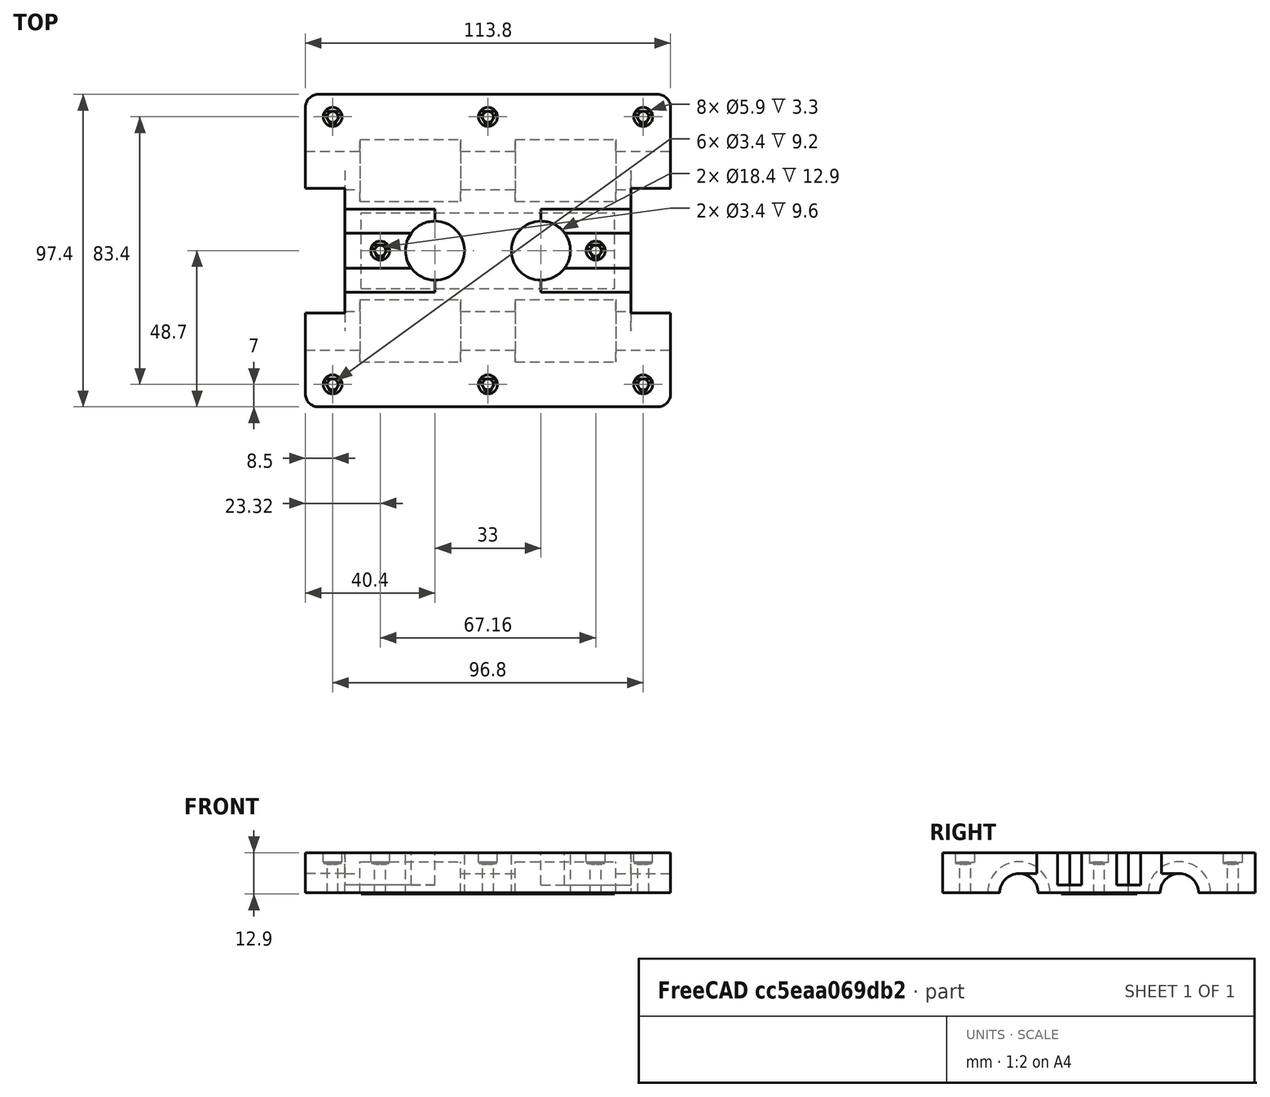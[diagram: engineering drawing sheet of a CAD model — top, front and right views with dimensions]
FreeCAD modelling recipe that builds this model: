
FCSTD DOCUMENT  (FreeCAD 0.17R13541 (Git))
Label: Carrito Parte superior
License: All rights reserved
LicenseURL: http://en.wikipedia.org/wiki/All_rights_reserved
objects: Part::Prism×42, Part::Cylinder×32, Part::MultiFuse×17, Part::Common×14, Part::Box×6, Part::Fuse×3, Part::FeaturePython×2, Part::Fillet×1, Part::Cut×1
note: 118 computed .brp shape members not serialized (recipe doc carries the construction recipe); baked Part::Feature solids carry a one-line shape summary decoded from their .brp

FEATURE [Part::Box] carhig_box
  AttacherType = Attacher::AttachEngine3D
  Height = 12.5
  Length = 113.8
  Placement = pos=(-56.9,-48.7,0) rot=(0,0,1;0rad)
  Width = 97.4
FEATURE [Part::Box] extrhold_higcar
  AttacherType = Attacher::AttachEngine3D
  Height = 1.4
  Length = 79
  Placement = pos=(-39.5,-11.8,12.1) rot=(0,0,1;0rad)
  Width = 23.6
FEATURE [Part::Cylinder] rod_n
  Angle = 360
  AttacherType = Attacher::AttachEngine3D
  Height = 115.8
  Placement = pos=(-57.9,-25,12.5) rot=(0,1,0;1.5708rad)
  Radius = 6
FEATURE [Part::Cylinder] bearing_1
  Angle = 360
  AttacherType = Attacher::AttachEngine3D
  Height = 31.4
  Placement = pos=(-39.9,25,12.5) rot=(0,1,0;1.5708rad)
  Radius = 9.7
FEATURE [Part::Cylinder] rod_p
  Angle = 360
  AttacherType = Attacher::AttachEngine3D
  Height = 115.8
  Placement = pos=(-57.9,25,12.5) rot=(0,1,0;1.5708rad)
  Radius = 6
FEATURE [Part::Cylinder] bearing_0
  Angle = 360
  AttacherType = Attacher::AttachEngine3D
  Height = 31.4
  Placement = pos=(8.5,25,12.5) rot=(0,1,0;1.5708rad)
  Radius = 9.7
FEATURE [Part::Fillet] carhig_box_fllt
  Base = -> carhig_box
  Edges = 4 edges r=4: [Edge1,Edge3,Edge5,Edge7]
  Placement = pos=(0,0,12.5) rot=(0,0,1;0rad)
FEATURE [Part::Fuse] carghig_fuse
  Base = -> carhig_box_fllt
  Tool = -> extrhold_higcar
FEATURE [Part::Cylinder] m3_bolt_hole_bolt_head
  Angle = 360
  AttacherType = Attacher::AttachEngine3D
  Height = 4
  Placement = pos=(0,0,22) rot=(0,0,1;0rad)
  Radius = 2.95
FEATURE [Part::Cylinder] m3_bolt_hole_bolt_shank001
  Angle = 360
  AttacherType = Attacher::AttachEngine3D
  Height = 27
  Placement = pos=(0,0,-1) rot=(0,0,1;0rad)
  Radius = 1.7
FEATURE [Part::Cylinder] m3_bolt_hole_bolt_sup1away
  Angle = 360
  AttacherType = Attacher::AttachEngine3D
  Height = 3.3
  Placement = pos=(0,0,21.7) rot=(0,0,1;0rad)
  Radius = 2.95
FEATURE [Part::Cylinder] bearing_2
  Angle = 360
  AttacherType = Attacher::AttachEngine3D
  Height = 31.4
  Placement = pos=(8.5,-25,12.5) rot=(0,1,0;1.5708rad)
  Radius = 9.7
FEATURE [Part::Cylinder] higcar_fil_hole1
  Angle = 360
  AttacherType = Attacher::AttachEngine3D
  Height = 15.3
  Placement = pos=(16.5,0,10.7) rot=(0,0,1;0rad)
  Radius = 9.2
FEATURE [Part::Cylinder] bearing_3
  Angle = 360
  AttacherType = Attacher::AttachEngine3D
  Height = 31.4
  Placement = pos=(-39.9,-25,12.5) rot=(0,1,0;1.5708rad)
  Radius = 9.7
FEATURE [Part::Cylinder] higcar_fil_hole2
  Angle = 360
  AttacherType = Attacher::AttachEngine3D
  Height = 15.3
  Placement = pos=(-16.5,0,10.7) rot=(0,0,1;0rad)
  Radius = 9.2
FEATURE [Part::Cylinder] m3_bolt_hole_bolt_shank
  Angle = 360
  AttacherType = Attacher::AttachEngine3D
  Height = 27
  Placement = pos=(0,0,-1) rot=(0,0,1;0rad)
  Radius = 1.7
FEATURE [Part::Prism] m3_bolt_hole_bolt_sup2
  AttacherType = Attacher::AttachEngine3D
  Circumradius = 1.955
  Height = 3.6
  Placement = pos=(0,0,21.4) rot=(0,0,1;0rad)
  Polygon = 6
FEATURE [Part::Prism] m3_bolt_hole_bolt_sup1
  AttacherType = Attacher::AttachEngine3D
  Circumradius = 3.4
  Height = 3.3
  Placement = pos=(0,0,21.7) rot=(0,0,1;0.523599rad)
  Polygon = 3
FEATURE [Part::Common] sup1cut001
  Base = -> m3_bolt_hole_bolt_sup1
  Tool = -> m3_bolt_hole_bolt_sup1away
FEATURE [Part::MultiFuse] m3_bolt_hole_bolt
  Shapes = -> [m3_bolt_hole_bolt_shank,m3_bolt_hole_bolt_head,sup1cut001,m3_bolt_hole_bolt_sup2]
FEATURE [Part::Prism] m3_bolt_hole_nut001
  AttacherType = Attacher::AttachEngine3D
  Circumradius = 3.605
  Height = 3.8
  Placement = pos=(0,0,-1) rot=(0,0,1;0rad)
  Polygon = 6
FEATURE [Part::Prism] m3_bolt_hole_nut
  AttacherType = Attacher::AttachEngine3D
  Circumradius = 3.605
  Height = 3.8
  Placement = pos=(0,0,-1) rot=(0,0,1;0rad)
  Polygon = 6
FEATURE [Part::MultiFuse] boltnut001
  Placement = pos=(33.58,0,0) rot=(0,0,1;0rad)
  Shapes = -> [m3_bolt_hole_bolt,m3_bolt_hole_nut]
FEATURE [Part::Prism] m3_bolt_hole_bolt_sup2001
  AttacherType = Attacher::AttachEngine3D
  Circumradius = 1.955
  Height = 3.6
  Placement = pos=(0,0,21.4) rot=(0,0,1;0rad)
  Polygon = 6
FEATURE [Part::Prism] m3_bolt_hole_bolt_sup1001
  AttacherType = Attacher::AttachEngine3D
  Circumradius = 3.4
  Height = 3.3
  Placement = pos=(0,0,21.7) rot=(0,0,1;0.523599rad)
  Polygon = 3
FEATURE [Part::Cylinder] m3_bolt_hole_bolt_head004
  Angle = 360
  AttacherType = Attacher::AttachEngine3D
  Height = 4
  Placement = pos=(0,0,22) rot=(0,0,1;0rad)
  Radius = 2.95
FEATURE [Part::Cylinder] m3_bolt_hole_bolt_head001
  Angle = 360
  AttacherType = Attacher::AttachEngine3D
  Height = 4
  Placement = pos=(0,0,22) rot=(0,0,1;0rad)
  Radius = 2.95
FEATURE [Part::Cylinder] m3_bolt_hole_bolt_head002
  Angle = 360
  AttacherType = Attacher::AttachEngine3D
  Height = 4
  Placement = pos=(0,0,22) rot=(0,0,1;0rad)
  Radius = 2.95
FEATURE [Part::Cylinder] m3_bolt_hole_bolt_sup1away002
  Angle = 360
  AttacherType = Attacher::AttachEngine3D
  Height = 3.3
  Placement = pos=(0,0,21.7) rot=(0,0,1;0rad)
  Radius = 2.95
FEATURE [Part::Cylinder] m3_bolt_hole_bolt_sup1away004
  Angle = 360
  AttacherType = Attacher::AttachEngine3D
  Height = 3.3
  Placement = pos=(0,0,21.7) rot=(0,0,1;0rad)
  Radius = 2.95
FEATURE [Part::Cylinder] m3_bolt_hole_bolt_shank002
  Angle = 360
  AttacherType = Attacher::AttachEngine3D
  Height = 27
  Placement = pos=(0,0,-1) rot=(0,0,1;0rad)
  Radius = 1.7
FEATURE [Part::Cylinder] m3_bolt_hole_bolt_sup1away003
  Angle = 360
  AttacherType = Attacher::AttachEngine3D
  Height = 3.3
  Placement = pos=(0,0,21.7) rot=(0,0,1;0rad)
  Radius = 2.95
FEATURE [Part::Cylinder] m3_bolt_hole_bolt_head003
  Angle = 360
  AttacherType = Attacher::AttachEngine3D
  Height = 4
  Placement = pos=(0,0,22) rot=(0,0,1;0rad)
  Radius = 2.95
FEATURE [Part::Cylinder] m3_bolt_hole_bolt_sup1away001
  Angle = 360
  AttacherType = Attacher::AttachEngine3D
  Height = 3.3
  Placement = pos=(0,0,21.7) rot=(0,0,1;0rad)
  Radius = 2.95
FEATURE [Part::Common] sup1cut002
  Base = -> m3_bolt_hole_bolt_sup1001
  Tool = -> m3_bolt_hole_bolt_sup1away001
FEATURE [Part::MultiFuse] m3_bolt_hole_bolt001
  Shapes = -> [m3_bolt_hole_bolt_shank001,m3_bolt_hole_bolt_head001,sup1cut002,m3_bolt_hole_bolt_sup2001]
FEATURE [Part::MultiFuse] boltnut002
  Placement = pos=(-33.58,0,0) rot=(0,0,1;0rad)
  Shapes = -> [m3_bolt_hole_bolt001,m3_bolt_hole_nut001]
FEATURE [Part::Cylinder] m3_bolt_hole_bolt_shank004
  Angle = 360
  AttacherType = Attacher::AttachEngine3D
  Height = 27
  Placement = pos=(0,0,-1) rot=(0,0,1;0rad)
  Radius = 1.7
FEATURE [Part::Cylinder] m3_bolt_hole_bolt_shank003
  Angle = 360
  AttacherType = Attacher::AttachEngine3D
  Height = 27
  Placement = pos=(0,0,-1) rot=(0,0,1;0rad)
  Radius = 1.7
FEATURE [Part::Prism] m3_bolt_hole_bolt_sup2002
  AttacherType = Attacher::AttachEngine3D
  Circumradius = 1.955
  Height = 3.6
  Placement = pos=(0,0,21.4) rot=(0,0,1;0rad)
  Polygon = 6
FEATURE [Part::Prism] m3_bolt_hole_nut002
  AttacherType = Attacher::AttachEngine3D
  Circumradius = 3.605
  Height = 3.8
  Placement = pos=(0,0,-1) rot=(0,0,1;0rad)
  Polygon = 6
FEATURE [Part::Prism] m3_bolt_hole_supnut1away
  AttacherType = Attacher::AttachEngine3D
  Circumradius = 3.605
  Height = 3.1
  Polygon = 6
FEATURE [Part::Prism] m3_bolt_hole_nutsup1
  AttacherType = Attacher::AttachEngine3D
  Circumradius = 3.4
  Height = 3.1
  Placement = pos=(0,0,0) rot=(0,0,1;0.523599rad)
  Polygon = 3
FEATURE [Part::Common] supnut1_cut001
  Base = -> m3_bolt_hole_nutsup1
  Tool = -> m3_bolt_hole_supnut1away
FEATURE [Part::Prism] m3_bolt_hole_bolt_sup1002
  AttacherType = Attacher::AttachEngine3D
  Circumradius = 3.4
  Height = 3.3
  Placement = pos=(0,0,21.7) rot=(0,0,1;0.523599rad)
  Polygon = 3
FEATURE [Part::Common] sup1cut003
  Base = -> m3_bolt_hole_bolt_sup1002
  Tool = -> m3_bolt_hole_bolt_sup1away002
FEATURE [Part::MultiFuse] m3_bolt_hole_bolt002
  Shapes = -> [m3_bolt_hole_bolt_shank002,m3_bolt_hole_bolt_head002,sup1cut003,m3_bolt_hole_bolt_sup2002]
FEATURE [Part::Prism] m3_bolt_hole_bolt_sup1003
  AttacherType = Attacher::AttachEngine3D
  Circumradius = 3.4
  Height = 3.3
  Placement = pos=(0,0,21.7) rot=(0,0,1;0.523599rad)
  Polygon = 3
FEATURE [Part::Common] sup1cut004
  Base = -> m3_bolt_hole_bolt_sup1003
  Tool = -> m3_bolt_hole_bolt_sup1away003
FEATURE [Part::Prism] m3_bolt_hole_bolt_sup2003
  AttacherType = Attacher::AttachEngine3D
  Circumradius = 1.955
  Height = 3.6
  Placement = pos=(0,0,21.4) rot=(0,0,1;0rad)
  Polygon = 6
FEATURE [Part::MultiFuse] m3_bolt_hole_bolt003
  Shapes = -> [m3_bolt_hole_bolt_shank003,m3_bolt_hole_bolt_head003,sup1cut004,m3_bolt_hole_bolt_sup2003]
FEATURE [Part::Prism] m3_bolt_hole_nut003
  AttacherType = Attacher::AttachEngine3D
  Circumradius = 3.605
  Height = 3.8
  Placement = pos=(0,0,-1) rot=(0,0,1;0rad)
  Polygon = 6
FEATURE [Part::Prism] m3_bolt_hole_supnut2
  AttacherType = Attacher::AttachEngine3D
  Circumradius = 1.955
  Height = 3.4
  Polygon = 6
FEATURE [Part::MultiFuse] boltnut003
  Placement = pos=(48.4,41.7,0) rot=(0,0,1;0rad)
  Shapes = -> [m3_bolt_hole_bolt002,m3_bolt_hole_nut002,supnut1_cut001,m3_bolt_hole_supnut2]
FEATURE [Part::Prism] m3_bolt_hole_supnut2001
  AttacherType = Attacher::AttachEngine3D
  Circumradius = 1.955
  Height = 3.4
  Polygon = 6
FEATURE [Part::Prism] m3_bolt_hole_supnut1away001
  AttacherType = Attacher::AttachEngine3D
  Circumradius = 3.605
  Height = 3.1
  Polygon = 6
FEATURE [Part::Prism] m3_bolt_hole_nutsup1001
  AttacherType = Attacher::AttachEngine3D
  Circumradius = 3.4
  Height = 3.1
  Placement = pos=(0,0,0) rot=(0,0,1;0.523599rad)
  Polygon = 3
FEATURE [Part::Common] supnut1_cut002
  Base = -> m3_bolt_hole_nutsup1001
  Tool = -> m3_bolt_hole_supnut1away001
FEATURE [Part::MultiFuse] boltnut004
  Placement = pos=(0,41.7,0) rot=(0,0,1;0rad)
  Shapes = -> [m3_bolt_hole_bolt003,m3_bolt_hole_nut003,supnut1_cut002,m3_bolt_hole_supnut2001]
FEATURE [Part::Prism] m3_bolt_hole_bolt_sup1004
  AttacherType = Attacher::AttachEngine3D
  Circumradius = 3.4
  Height = 3.3
  Placement = pos=(0,0,21.7) rot=(0,0,1;0.523599rad)
  Polygon = 3
FEATURE [Part::Common] sup1cut005
  Base = -> m3_bolt_hole_bolt_sup1004
  Tool = -> m3_bolt_hole_bolt_sup1away004
FEATURE [Part::Prism] m3_bolt_hole_bolt_sup2004
  AttacherType = Attacher::AttachEngine3D
  Circumradius = 1.955
  Height = 3.6
  Placement = pos=(0,0,21.4) rot=(0,0,1;0rad)
  Polygon = 6
FEATURE [Part::MultiFuse] m3_bolt_hole_bolt004
  Shapes = -> [m3_bolt_hole_bolt_shank004,m3_bolt_hole_bolt_head004,sup1cut005,m3_bolt_hole_bolt_sup2004]
FEATURE [Part::Prism] m3_bolt_hole_supnut1away002
  AttacherType = Attacher::AttachEngine3D
  Circumradius = 3.605
  Height = 3.1
  Polygon = 6
FEATURE [Part::Prism] m3_bolt_hole_supnut2002
  AttacherType = Attacher::AttachEngine3D
  Circumradius = 1.955
  Height = 3.4
  Polygon = 6
FEATURE [Part::Prism] m3_bolt_hole_nut004
  AttacherType = Attacher::AttachEngine3D
  Circumradius = 3.605
  Height = 3.8
  Placement = pos=(0,0,-1) rot=(0,0,1;0rad)
  Polygon = 6
FEATURE [Part::Prism] m3_bolt_hole_bolt_sup1005
  AttacherType = Attacher::AttachEngine3D
  Circumradius = 3.4
  Height = 3.3
  Placement = pos=(0,0,21.7) rot=(0,0,1;0.523599rad)
  Polygon = 3
FEATURE [Part::Prism] m3_bolt_hole_nutsup1002
  AttacherType = Attacher::AttachEngine3D
  Circumradius = 3.4
  Height = 3.1
  Placement = pos=(0,0,0) rot=(0,0,1;0.523599rad)
  Polygon = 3
FEATURE [Part::Common] supnut1_cut003
  Base = -> m3_bolt_hole_nutsup1002
  Tool = -> m3_bolt_hole_supnut1away002
FEATURE [Part::MultiFuse] boltnut005
  Placement = pos=(-48.4,41.7,0) rot=(0,0,1;0rad)
  Shapes = -> [m3_bolt_hole_bolt004,m3_bolt_hole_nut004,supnut1_cut003,m3_bolt_hole_supnut2002]
FEATURE [Part::Cylinder] m3_bolt_hole_bolt_head005
  Angle = 360
  AttacherType = Attacher::AttachEngine3D
  Height = 4
  Placement = pos=(0,0,22) rot=(0,0,1;0rad)
  Radius = 2.95
FEATURE [Part::Cylinder] m3_bolt_hole_bolt_sup1away006
  Angle = 360
  AttacherType = Attacher::AttachEngine3D
  Height = 3.3
  Placement = pos=(0,0,21.7) rot=(0,0,1;0rad)
  Radius = 2.95
FEATURE [Part::Cylinder] m3_bolt_hole_bolt_head007
  Angle = 360
  AttacherType = Attacher::AttachEngine3D
  Height = 4
  Placement = pos=(0,0,22) rot=(0,0,1;0rad)
  Radius = 2.95
FEATURE [Part::Cylinder] m3_bolt_hole_bolt_sup1away007
  Angle = 360
  AttacherType = Attacher::AttachEngine3D
  Height = 3.3
  Placement = pos=(0,0,21.7) rot=(0,0,1;0rad)
  Radius = 2.95
FEATURE [Part::Cylinder] m3_bolt_hole_bolt_shank005
  Angle = 360
  AttacherType = Attacher::AttachEngine3D
  Height = 27
  Placement = pos=(0,0,-1) rot=(0,0,1;0rad)
  Radius = 1.7
FEATURE [Part::Cylinder] m3_bolt_hole_bolt_sup1away005
  Angle = 360
  AttacherType = Attacher::AttachEngine3D
  Height = 3.3
  Placement = pos=(0,0,21.7) rot=(0,0,1;0rad)
  Radius = 2.95
FEATURE [Part::Common] sup1cut006
  Base = -> m3_bolt_hole_bolt_sup1005
  Tool = -> m3_bolt_hole_bolt_sup1away005
FEATURE [Part::Cylinder] m3_bolt_hole_bolt_shank006
  Angle = 360
  AttacherType = Attacher::AttachEngine3D
  Height = 27
  Placement = pos=(0,0,-1) rot=(0,0,1;0rad)
  Radius = 1.7
FEATURE [Part::Cylinder] m3_bolt_hole_bolt_head006
  Angle = 360
  AttacherType = Attacher::AttachEngine3D
  Height = 4
  Placement = pos=(0,0,22) rot=(0,0,1;0rad)
  Radius = 2.95
FEATURE [Part::Cylinder] m3_bolt_hole_bolt_shank007
  Angle = 360
  AttacherType = Attacher::AttachEngine3D
  Height = 27
  Placement = pos=(0,0,-1) rot=(0,0,1;0rad)
  Radius = 1.7
FEATURE [Part::Prism] m3_bolt_hole_nut005
  AttacherType = Attacher::AttachEngine3D
  Circumradius = 3.605
  Height = 3.8
  Placement = pos=(0,0,-1) rot=(0,0,1;0rad)
  Polygon = 6
FEATURE [Part::Prism] m3_bolt_hole_supnut1away003
  AttacherType = Attacher::AttachEngine3D
  Circumradius = 3.605
  Height = 3.1
  Polygon = 6
FEATURE [Part::Prism] m3_bolt_hole_supnut2003
  AttacherType = Attacher::AttachEngine3D
  Circumradius = 1.955
  Height = 3.4
  Polygon = 6
FEATURE [Part::Prism] m3_bolt_hole_nutsup1003
  AttacherType = Attacher::AttachEngine3D
  Circumradius = 3.4
  Height = 3.1
  Placement = pos=(0,0,0) rot=(0,0,1;0.523599rad)
  Polygon = 3
FEATURE [Part::Common] supnut1_cut004
  Base = -> m3_bolt_hole_nutsup1003
  Tool = -> m3_bolt_hole_supnut1away003
FEATURE [Part::Prism] m3_bolt_hole_bolt_sup2005
  AttacherType = Attacher::AttachEngine3D
  Circumradius = 1.955
  Height = 3.6
  Placement = pos=(0,0,21.4) rot=(0,0,1;0rad)
  Polygon = 6
FEATURE [Part::MultiFuse] m3_bolt_hole_bolt005
  Shapes = -> [m3_bolt_hole_bolt_shank005,m3_bolt_hole_bolt_head005,sup1cut006,m3_bolt_hole_bolt_sup2005]
FEATURE [Part::MultiFuse] boltnut006
  Placement = pos=(48.4,-41.7,0) rot=(0,0,1;0rad)
  Shapes = -> [m3_bolt_hole_bolt005,m3_bolt_hole_nut005,supnut1_cut004,m3_bolt_hole_supnut2003]
FEATURE [Part::Prism] m3_bolt_hole_nutsup1004
  AttacherType = Attacher::AttachEngine3D
  Circumradius = 3.4
  Height = 3.1
  Placement = pos=(0,0,0) rot=(0,0,1;0.523599rad)
  Polygon = 3
FEATURE [Part::Prism] m3_bolt_hole_bolt_sup1006
  AttacherType = Attacher::AttachEngine3D
  Circumradius = 3.4
  Height = 3.3
  Placement = pos=(0,0,21.7) rot=(0,0,1;0.523599rad)
  Polygon = 3
FEATURE [Part::Common] sup1cut007
  Base = -> m3_bolt_hole_bolt_sup1006
  Tool = -> m3_bolt_hole_bolt_sup1away006
FEATURE [Part::Prism] m3_bolt_hole_bolt_sup2006
  AttacherType = Attacher::AttachEngine3D
  Circumradius = 1.955
  Height = 3.6
  Placement = pos=(0,0,21.4) rot=(0,0,1;0rad)
  Polygon = 6
FEATURE [Part::MultiFuse] m3_bolt_hole_bolt006
  Shapes = -> [m3_bolt_hole_bolt_shank006,m3_bolt_hole_bolt_head006,sup1cut007,m3_bolt_hole_bolt_sup2006]
FEATURE [Part::Prism] m3_bolt_hole_nut006
  AttacherType = Attacher::AttachEngine3D
  Circumradius = 3.605
  Height = 3.8
  Placement = pos=(0,0,-1) rot=(0,0,1;0rad)
  Polygon = 6
FEATURE [Part::Prism] m3_bolt_hole_supnut1away004
  AttacherType = Attacher::AttachEngine3D
  Circumradius = 3.605
  Height = 3.1
  Polygon = 6
FEATURE [Part::Common] supnut1_cut005
  Base = -> m3_bolt_hole_nutsup1004
  Tool = -> m3_bolt_hole_supnut1away004
FEATURE [Part::Prism] m3_bolt_hole_bolt_sup2007
  AttacherType = Attacher::AttachEngine3D
  Circumradius = 1.955
  Height = 3.6
  Placement = pos=(0,0,21.4) rot=(0,0,1;0rad)
  Polygon = 6
FEATURE [Part::Prism] m3_bolt_hole_nut007
  AttacherType = Attacher::AttachEngine3D
  Circumradius = 3.605
  Height = 3.8
  Placement = pos=(0,0,-1) rot=(0,0,1;0rad)
  Polygon = 6
FEATURE [Part::Prism] m3_bolt_hole_supnut2004
  AttacherType = Attacher::AttachEngine3D
  Circumradius = 1.955
  Height = 3.4
  Polygon = 6
FEATURE [Part::MultiFuse] boltnut007
  Placement = pos=(0,-41.7,0) rot=(0,0,1;0rad)
  Shapes = -> [m3_bolt_hole_bolt006,m3_bolt_hole_nut006,supnut1_cut005,m3_bolt_hole_supnut2004]
FEATURE [Part::Prism] m3_bolt_hole_bolt_sup1007
  AttacherType = Attacher::AttachEngine3D
  Circumradius = 3.4
  Height = 3.3
  Placement = pos=(0,0,21.7) rot=(0,0,1;0.523599rad)
  Polygon = 3
FEATURE [Part::Common] sup1cut008
  Base = -> m3_bolt_hole_bolt_sup1007
  Tool = -> m3_bolt_hole_bolt_sup1away007
FEATURE [Part::MultiFuse] m3_bolt_hole_bolt007
  Shapes = -> [m3_bolt_hole_bolt_shank007,m3_bolt_hole_bolt_head007,sup1cut008,m3_bolt_hole_bolt_sup2007]
FEATURE [Part::Prism] m3_bolt_hole_nutsup1005
  AttacherType = Attacher::AttachEngine3D
  Circumradius = 3.4
  Height = 3.1
  Placement = pos=(0,0,0) rot=(0,0,1;0.523599rad)
  Polygon = 3
FEATURE [Part::Prism] m3_bolt_hole_supnut2005
  AttacherType = Attacher::AttachEngine3D
  Circumradius = 1.955
  Height = 3.4
  Polygon = 6
FEATURE [Part::Prism] m3_bolt_hole_supnut1away005
  AttacherType = Attacher::AttachEngine3D
  Circumradius = 3.605
  Height = 3.1
  Polygon = 6
FEATURE [Part::Common] supnut1_cut006
  Base = -> m3_bolt_hole_nutsup1005
  Tool = -> m3_bolt_hole_supnut1away005
FEATURE [Part::MultiFuse] boltnut008
  Placement = pos=(-48.4,-41.7,0) rot=(0,0,1;0rad)
  Shapes = -> [m3_bolt_hole_bolt007,m3_bolt_hole_nut007,supnut1_cut006,m3_bolt_hole_supnut2005]
FEATURE [Part::Box] bccr_box_of_clean
  AttacherType = Attacher::AttachEngine3D
  Height = 6
  Length = 41
  Placement = pos=(44.6,-25,12.5) rot=(0,0,1;0rad)
  Width = 50
FEATURE [Part::Box] highcar_lscrew_hole1
  AttacherType = Attacher::AttachEngine3D
  Height = 11
  Length = 29.1
  Placement = pos=(16.5,-12.9542,15) rot=(0,0,1;0rad)
  Width = 7.5
FEATURE [Part::Box] highcar_lscrew_hole0
  AttacherType = Attacher::AttachEngine3D
  Height = 11
  Length = 29.1
  Placement = pos=(16.5,5.45417,15) rot=(0,0,1;0rad)
  Width = 7.5
FEATURE [Part::Fuse] higcar_lscrew_fuse
  Base = -> highcar_lscrew_hole0
  Tool = -> highcar_lscrew_hole1
FEATURE [Part::FeaturePython] Clone001  label="Clone of higcar_lscrew_fuse"  # Draft clone (typed FeaturePython)
  Objects = -> [higcar_lscrew_fuse]
  Placement = pos=(0,0,0) rot=(0,0,1;3.14159rad)
  Scale = (1,1,1)
FEATURE [Part::Box] bccr_box001
  AttacherType = Attacher::AttachEngine3D
  Height = 25
  Length = 41
  Placement = pos=(44.6,-19.4,0) rot=(0,0,1;0rad)
  Width = 38.8
FEATURE [Part::Fuse] fuse_bccr_box_of
  Base = -> bccr_box001
  Tool = -> bccr_box_of_clean
FEATURE [Part::FeaturePython] Clone  label="Clone of fuse_bccr_box_of"  # Draft clone (typed FeaturePython)
  Objects = -> [fuse_bccr_box_of]
  Placement = pos=(0,0,0) rot=(0,0,1;3.14159rad)
  Scale = (1,1,1)
FEATURE [Part::MultiFuse] fuse_higcar_holes
  Shapes = -> [rod_n,rod_p,bearing_0,bearing_1,bearing_2,bearing_3,higcar_fil_hole1,higcar_fil_hole2,boltnut001,boltnut002,boltnut003,boltnut004,boltnut005,boltnut006,boltnut007,boltnut008,fuse_bccr_box_of,Clone,higcar_lscrew_fuse,Clone001]
FEATURE [Part::Cut] higcar_hole
  Base = -> carghig_fuse
  Placement = pos=(0,0,30) rot=(0,0,1;0rad)
  Tool = -> fuse_higcar_holes
